# Revit family: Fireplace_Wood_Heatilator_MultiSided-See-Thru
name_source: partatom
category: Mechanical Equipment
revit_build: Autodesk Revit 2015 (Build: 20140323_1530(x64)
units: mm (PartAtom-declared; Revit-internal decimal feet)

## types (4) — shared parameters
Assembly Code = D3020
Construction Details = http://www.arcat.com
Default Elevation = 0' - 0"
Fixture Finish = Metal - Heatilator - Metallic Black
Fuel Consumption = as Specified
HVAC_BTU Output = 0.0 Btu/h
Heating Capacity = as Specified
Keynote = 10305
Manufacturer = Heatilator
Manufacturer Website = http://www.heatilator.com
Product Data = http://www.arcat.com
Revision = R2_2014-09
Sales Information = http://www.heatilator.com
Send Message = http://www.arcat.com
Specification = http://www.arcat.com
Standards Conformance = UL  ;  cUL
URL = http://www.heatilator.com
Unit Depth = 2' - 0"
zero-valued in all types: Expected Lifespan (Years), Maintenance Schedule (Months), Unit Weight, Warranty Duration (Years)

## per-type parameters (varying)
| type | Box Height | Description | Efficiency Ratings | Fuel Type | HVAC_BTU Input | Model | Opening Height | Opening Width | Unit Height | Unit Width |
| 42x23 Viewing Area Gas Log | 3' - 2 3/8" | Heatilator Gas Burning Fireplace - MultiSided ST42A as Specified | as Specified | NG | 100000.0 Btu/h | ST42A Gas | 1' - 11" | 3' - 6" | 4' - 10 7/8" | 3' - 11" |
| 36x21 Viewing Area Gas Log | 2' - 11" | Heatilator Gas Burning Fireplace - MultiSided ST36D as Specified | as Specified | NG | 100000.0 Btu/h | ST36D Gas | 1' - 8 7/8" | 3' - 0" | 3' - 11 1/4" | 3' - 4" |
| 42x23 Viewing Area Wood | 3' - 2 3/8" | Heatilator Wood Burning Fireplace - MultiSided ST42A as Specified | Determined by Wood Used | Wood | 0.0 Btu/h | ST42A | 1' - 11" | 3' - 6" | 4' - 10 7/8" | 3' - 11" |
| 36x21 Viewing Area Wood | 2' - 11" | Heatilator Wood Burning Fireplace - MultiSided ST36D as Specified | Determined by Wood Used | Wood | 0.0 Btu/h | ST36D | 1' - 8 7/8" | 3' - 0" | 3' - 11 1/4" | 3' - 4" |

## geometry (parser evidence)
native form markers: Blend x4, Sweep x4
no freeform markers — native parametric forms only
